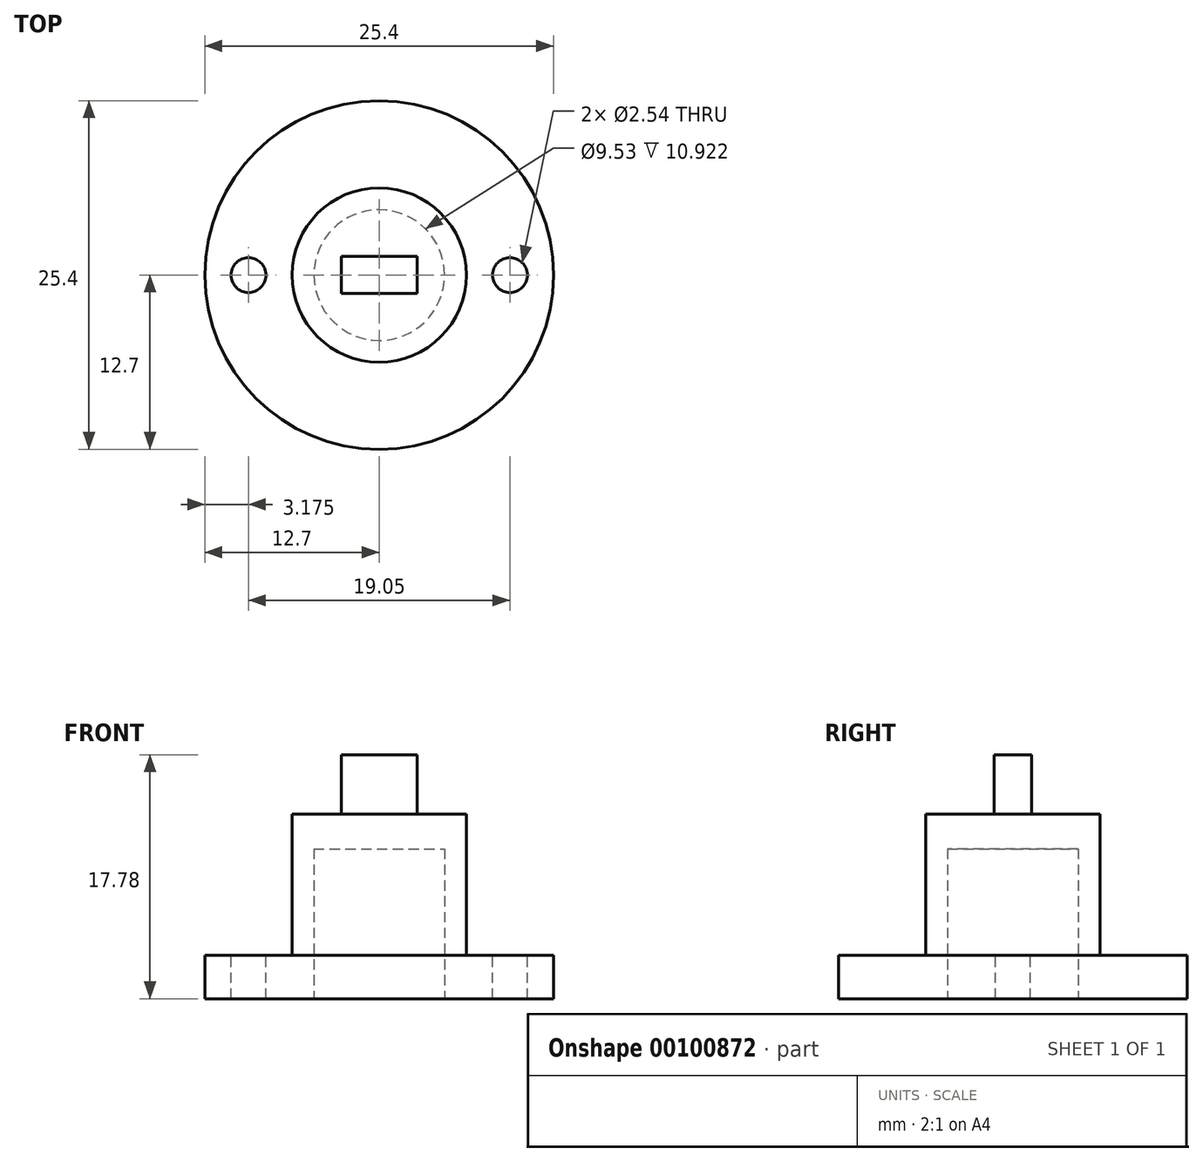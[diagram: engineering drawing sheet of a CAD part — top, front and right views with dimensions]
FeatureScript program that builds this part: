
annotation { "Feature Type Name" : "Feature", "Feature Type Description" : "" }
export const myFeature = defineFeature(function(context is Context, id is Id, definition is map)
    precondition{}
    {
        {
            var Q0;
            Q0=qCreatedBy(makeId("Front.planeOp"),FACE);
            var sketch = newSketch(context, id + "F0", { "sketchPlane" : qUnion([Q0])});
            skLineSegment(sketch, "E0", {"start": v(0, 13.46) * mm, "end": v(6.35, 13.46) * mm});
            skLineSegment(sketch, "E1", {"start": v(6.35, 13.46) * mm, "end": v(6.35, 3.17) * mm});
            skLineSegment(sketch, "E2", {"start": v(6.35, 3.17) * mm, "end": v(12.7, 3.17) * mm});
            skLineSegment(sketch, "E3", {"start": v(12.7, 3.18) * mm, "end": v(12.7, 0) * mm});
            skLineSegment(sketch, "E4", {"start": v(12.7, 0) * mm, "end": v(4.76, 0) * mm});
            skLineSegment(sketch, "E5", {"start": v(4.76, 0) * mm, "end": v(4.76, 10.92) * mm});
            skLineSegment(sketch, "E6", {"start": v(4.76, 10.92) * mm, "end": v(0, 10.92) * mm});
            skLineSegment(sketch, "E7", {"start": v(0, 10.92) * mm, "end": v(0, 13.46) * mm});
            skSolve(sketch);
        }
        {
            var Q0;
            Q0 = qSketchRegion(id + "F0", true);
            var Q1;
            Q1=sQuery(id+"F0.wireOp",EDGE,"E7");
            revolve(context, id + "F1", {"entities" : qUnion([Q0]), "axis" : qUnion([Q1]), "revolveType" : RevolveType.FULL});
        }
        {
            var Q0;
            Q0=makeQuery(id+"F1.opRevolve","SWEPT_FACE",FACE,{"disambiguationData":[OSD([sQuery(id+"F0.wireOp",EDGE,"E0")])]});
            var sketch = newSketch(context, id + "F2", { "sketchPlane" : qUnion([Q0])});
            skLineSegment(sketch, "E8.bottom", {"start": v(2.76, 1.35) * mm, "end": v(-2.76, 1.35) * mm});
            skLineSegment(sketch, "E8.top", {"start": v(2.76, -1.35) * mm, "end": v(-2.76, -1.35) * mm});
            skLineSegment(sketch, "E8.left", {"start": v(2.76, 1.35) * mm, "end": v(2.76, -1.35) * mm});
            skLineSegment(sketch, "E8.right", {"start": v(-2.76, 1.35) * mm, "end": v(-2.76, -1.35) * mm});
            skPoint(sketch, "E8.middle", {"position": v(0, 0) * mm});
            skSolve(sketch);
        }
        {
            var Q0;
            Q0 = qSketchRegion(id + "F2", true);
            extrude(context, id + "F3", {"entities" : qUnion([Q0]), "operationType" : NewBodyOperationType.ADD, "depth" : 4.32 * mm});
        }
        {
            var Q0;
            Q0=makeQuery(id+"F1.opRevolve","SWEPT_FACE",FACE,{"disambiguationData":[OSD([sQuery(id+"F0.wireOp",EDGE,"E2")])]});
            var sketch = newSketch(context, id + "F4", { "sketchPlane" : qUnion([Q0])});
            skCircle(sketch, "E9", {"center": v(-9.53, 0) * mm, "radius": 1.27 * mm});
            skCircle(sketch, "E10", {"center": v(9.53, 0) * mm, "radius": 1.27 * mm});
            skLineSegment(sketch, "E11", {"start": v(9.53, 0) * mm, "end": v(0, 0) * mm, "construction": true});
            skLineSegment(sketch, "E12", {"start": v(0, 0) * mm, "end": v(-9.53, 0) * mm, "construction": true});
            skSolve(sketch);
        }
        {
            var Q0;
            Q0=makeQuery(id+"F4.imprint","IMPRINT",FACE,{"disambiguationData":[TD([[makeQuery(id+"F4.imprint","IMPRINT",EDGE,{"derivedFrom":sQuery(id+"F4.wireOp",EDGE,"E9")}),1.0]])]});
            var Q1;
            Q1=makeQuery(id+"F4.imprint","IMPRINT",FACE,{"disambiguationData":[TD([[makeQuery(id+"F4.imprint","IMPRINT",EDGE,{"derivedFrom":sQuery(id+"F4.wireOp",EDGE,"E10")}),1.0]])]});
            extrude(context, id + "F5", {"entities" : qUnion([Q0, Q1]), "operationType" : NewBodyOperationType.REMOVE, "endBound" : BoundingType.THROUGH_ALL, "oppositeDirection" : true, "depth" : 25.4 * mm});
        }
    });
